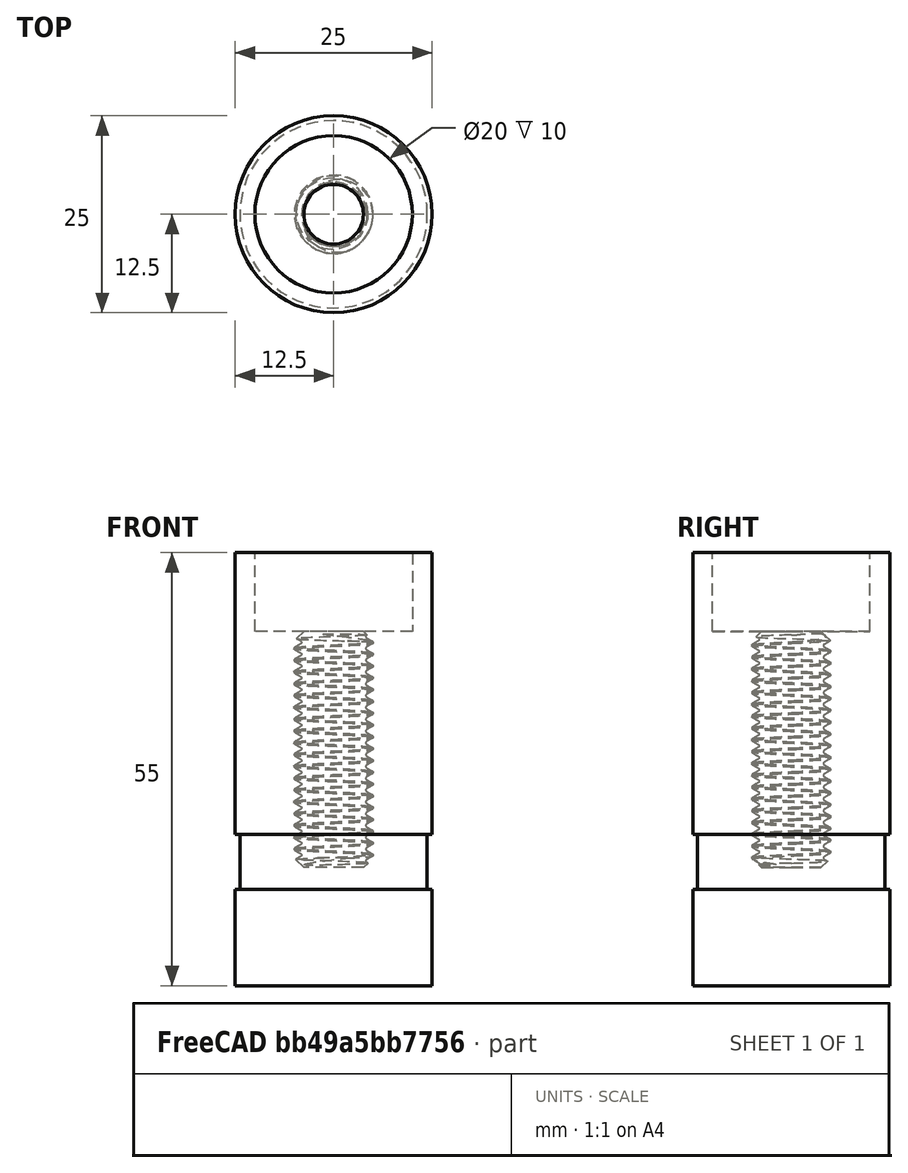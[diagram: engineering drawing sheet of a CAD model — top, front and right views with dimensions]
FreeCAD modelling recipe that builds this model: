
FCSTD DOCUMENT  (FreeCAD 0.19R24291 (Git))
Label: TMS_coil2chair_adaptor
License: All rights reserved
LicenseURL: http://en.wikipedia.org/wiki/All_rights_reserved
objects: Sketcher::SketchObject×4, PartDesign::Pad×2, Part::FeaturePython×1, PartDesign::Groove×1, PartDesign::Pocket×1, PartDesign::Body×1, Part::Cut×1
note: 15 computed .brp shape members not serialized (recipe doc carries the construction recipe); baked Part::Feature solids carry a one-line shape summary decoded from their .brp

FEATURE [Part::FeaturePython] ThreadedRod  label="M10x30.0-ThreadedRod"  # Fasteners workbench fastener (typed FeaturePython)
  Placement = pos=(0,0,20) rot=(0,0,1;0rad)
  diameter = 10
  invert = false
  length = 30
  matchOuter = false
  offset = 0
  thread = true
FEATURE [Sketcher::SketchObject] Sketch
  FullyConstrained = true
  MapMode = 5
  Support = -> [XY_Plane]
  sketch-geometry (1):
    g0: Circle CenterX=0 CenterY=0 CenterZ=0 NormalX=0 NormalY=0 NormalZ=1 AngleXU=0 Radius=12.5
  constraints (2):
    c: Coincident(g0,g-1)
    c: Radius(g0) = 12.5
FEATURE [PartDesign::Pad] Pad
  Direction = (1,1,1)
  Length = 30
  Length2 = 100
  Profile = -> Sketch
  Refine = true
  Type = 0
FEATURE [Sketcher::SketchObject] Sketch001
  AttachmentOffset = pos=(0,0,-25) rot=(0,0,1;0rad)
  FullyConstrained = true
  MapMode = 5
  Placement = pos=(0,0,-25) rot=(0,0,1;0rad)
  Support = -> [XY_Plane]
  sketch-geometry (1):
    g0: Circle CenterX=0 CenterY=0 CenterZ=0 NormalX=0 NormalY=0 NormalZ=1 AngleXU=0 Radius=12.5
  constraints (2):
    c: Coincident(g0,g-1)
    c: Radius(g0) = 12.5
FEATURE [PartDesign::Pad] Pad001
  BaseFeature = -> Pad
  Direction = (1,1,1)
  Length = 25
  Length2 = 100
  Profile = -> Sketch001
  Refine = true
  Type = 0
FEATURE [Sketcher::SketchObject] Sketch002
  ExternalGeometry = -> [Pad001]
  FullyConstrained = false
  MapMode = 5
  Placement = pos=(0,0,0) rot=(1,0,0;1.5708rad)
  Support = -> [XZ_Plane]
  sketch-geometry (4):
    g0: LineSegment StartX=11.9 StartY=-5.8 StartZ=0 EndX=16.9 EndY=-5.8 EndZ=0
    g1: LineSegment StartX=16.9 StartY=-5.8 StartZ=0 EndX=16.9 EndY=-12.8 EndZ=0
    g2: LineSegment StartX=16.9 StartY=-12.8 StartZ=0 EndX=11.9 EndY=-12.8 EndZ=0
    g3: LineSegment StartX=11.9 StartY=-12.8 StartZ=0 EndX=11.9 EndY=-5.8 EndZ=0
  constraints (11):
    c: Coincident(g0,g1)
    c: Coincident(g1,g2)
    c: Coincident(g2,g3)
    c: Coincident(g3,g0)
    c: Horizontal(g0)
    c: Horizontal(g2)
    c: Vertical(g1)
    c: Vertical(g3)
    c: DistanceX(g-1,g0) = 11.9
    c: DistanceY(g3,g3) = 7
    c: DistanceX(g2,g2) = 5
FEATURE [PartDesign::Groove] Groove
  Angle = 360
  Axis = (0,-2e-16,1)
  Base = (0,0,0)
  BaseFeature = -> Pad001
  Profile = -> Sketch002
  ReferenceAxis = -> Sketch002 [V_Axis]
  Refine = true
FEATURE [Sketcher::SketchObject] Sketch003
  AttachmentOffset = pos=(0,0,30) rot=(0,0,1;0rad)
  FullyConstrained = true
  MapMode = 5
  Placement = pos=(0,0,30) rot=(0,0,1;0rad)
  Support = -> [XY_Plane]
  sketch-geometry (1):
    g0: Circle CenterX=0 CenterY=0 CenterZ=0 NormalX=0 NormalY=0 NormalZ=1 AngleXU=0 Radius=10
  constraints (2):
    c: Coincident(g0,g-1)
    c: Radius(g0) = 10
FEATURE [PartDesign::Pocket] Pocket
  BaseFeature = -> Groove
  Length = 10
  Length2 = 100
  Profile = -> Sketch003
  Refine = true
  Type = 0
FEATURE [PartDesign::Body] Body
  Group = -> [Sketch,Pad,Sketch001,Pad001,Sketch002,Groove,Sketch003,Pocket]
  Origin = -> Origin
  Tip = -> Pocket
FEATURE [Part::Cut] Cut
  Base = -> Body
  Refine = true
  Tool = -> ThreadedRod
